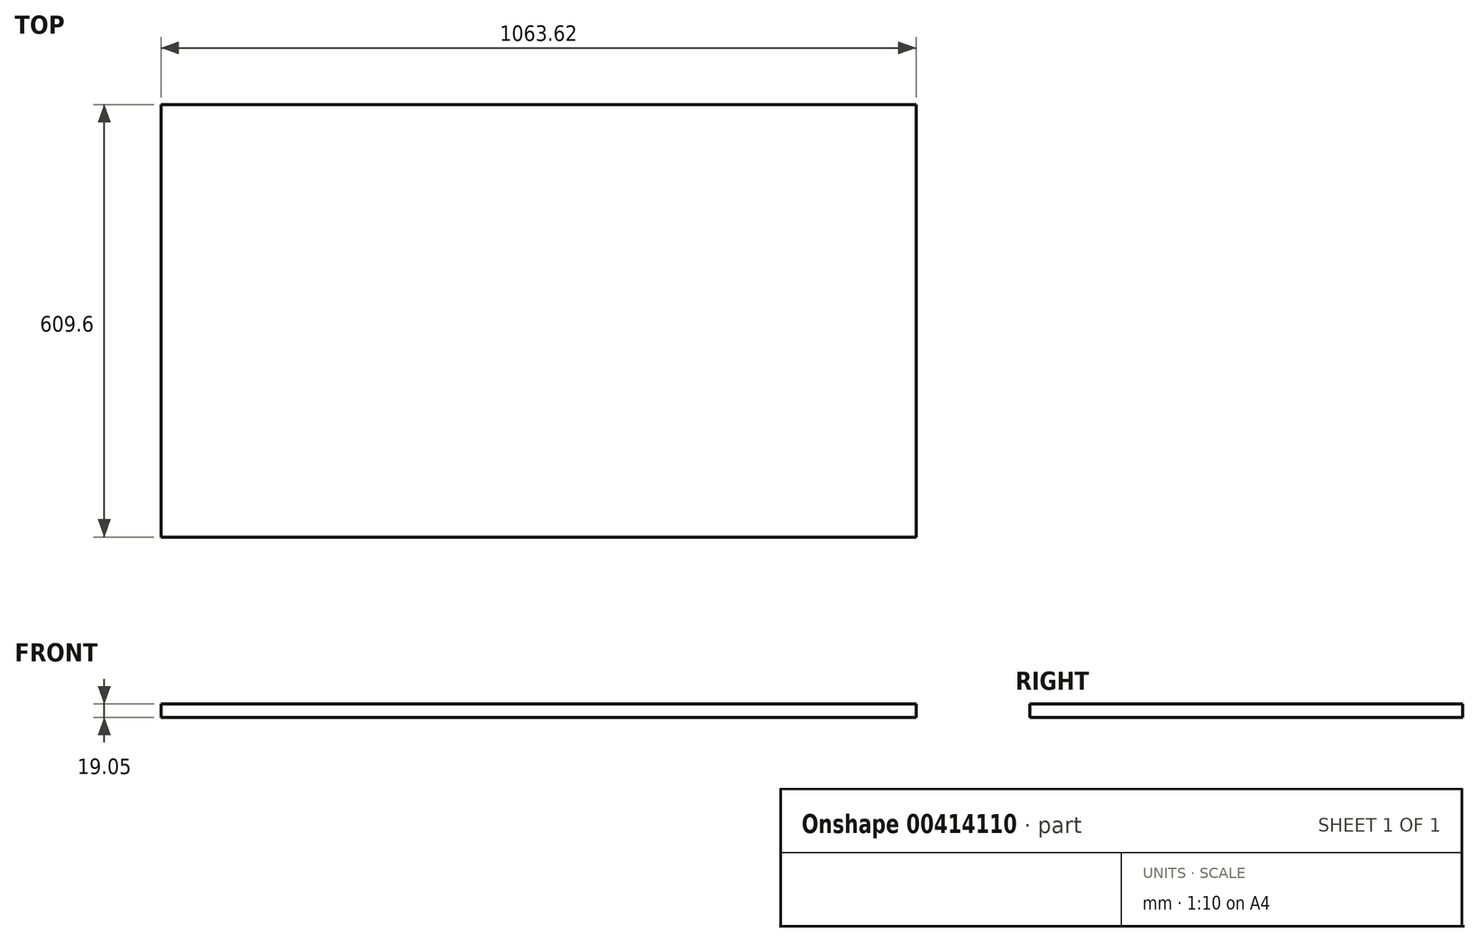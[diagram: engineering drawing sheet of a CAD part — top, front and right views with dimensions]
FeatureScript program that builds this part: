
annotation { "Feature Type Name" : "Feature", "Feature Type Description" : "" }
export const myFeature = defineFeature(function(context is Context, id is Id, definition is map)
    precondition{}
    {
        {
            var Q0;
            Q0=qCreatedBy(makeId("Top.planeOp"),FACE);
            var sketch = newSketch(context, id + "F0", { "sketchPlane" : qUnion([Q0])});
            skLineSegment(sketch, "E0.bottom", {"start": v(-531.81, 304.8) * mm, "end": v(531.81, 304.8) * mm});
            skLineSegment(sketch, "E0.top", {"start": v(-531.81, -304.8) * mm, "end": v(531.81, -304.8) * mm});
            skLineSegment(sketch, "E0.left", {"start": v(-531.81, 304.8) * mm, "end": v(-531.81, -304.8) * mm});
            skLineSegment(sketch, "E0.right", {"start": v(531.81, 304.8) * mm, "end": v(531.81, -304.8) * mm});
            skPoint(sketch, "E0.middle", {"position": v(0, 0) * mm});
            skSolve(sketch);
        }
        {
            var Q0;
            Q0=makeQuery(id+"F0.imprint","IMPRINT",FACE,{"disambiguationData":[TD([[makeQuery(id+"F0.imprint","IMPRINT",EDGE,{"derivedFrom":sQuery(id+"F0.wireOp",EDGE,"E0.bottom")}),-1.0]])]});
            extrude(context, id + "F1", {"entities" : qUnion([Q0]), "depth" : 19.05 * mm});
        }
    });
